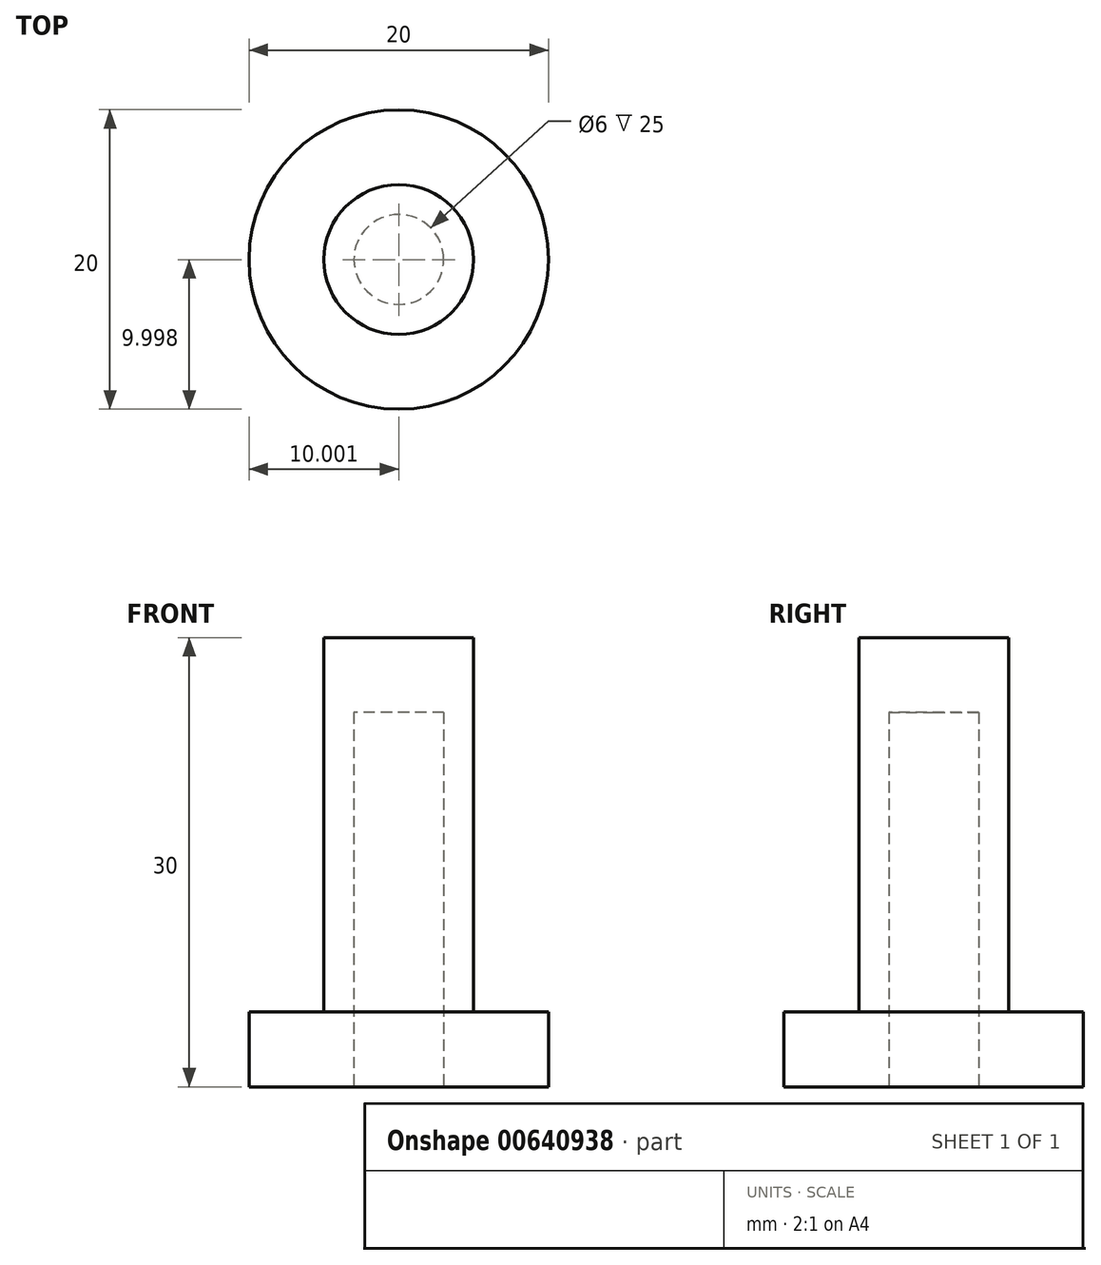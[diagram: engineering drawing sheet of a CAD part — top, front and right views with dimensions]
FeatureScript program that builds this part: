
annotation { "Feature Type Name" : "Feature", "Feature Type Description" : "" }
export const myFeature = defineFeature(function(context is Context, id is Id, definition is map)
    precondition{}
    {
        {
            var Q0;
            Q0=qCreatedBy(makeId("Top.planeOp"),FACE);
            var sketch = newSketch(context, id + "F0", { "sketchPlane" : qUnion([Q0])});
            skCircle(sketch, "E0", {"center": v(-26.7, 11.63) * mm, "radius": 3 * mm});
            skCircle(sketch, "E1", {"center": v(-26.7, 11.63) * mm, "radius": 5 * mm});
            skCircle(sketch, "E2", {"center": v(-26.7, 11.63) * mm, "radius": 10 * mm});
            skSolve(sketch);
        }
        {
            var Q0;
            Q0=makeQuery(id+"F0.imprint","IMPRINT",FACE,{"disambiguationData":[TD([[makeQuery(id+"F0.imprint","IMPRINT",EDGE,{"derivedFrom":sQuery(id+"F0.wireOp",EDGE,"E1")}),-1.0]])]});
            extrude(context, id + "F1", {"entities" : qUnion([Q0]), "depth" : 5 * mm, "offsetDistance" : 25 * mm});
        }
        {
            var Q0;
            Q0=makeQuery(id+"F0.imprint","IMPRINT",FACE,{"disambiguationData":[TD([[makeQuery(id+"F0.imprint","IMPRINT",EDGE,{"derivedFrom":sQuery(id+"F0.wireOp",EDGE,"E0")}),-1.0]])]});
            extrude(context, id + "F2", {"entities" : qUnion([Q0]), "operationType" : NewBodyOperationType.ADD, "depth" : 25 * mm, "offsetDistance" : 25 * mm});
        }
        {
            var Q0;
            Q0=makeQuery(id+"F2.opExtrude","CAP_FACE",FACE,{"disambiguationData":[OSD([sQuery(id+"F0.wireOp",EDGE,"E0"),sQuery(id+"F0.wireOp",EDGE,"E1")])],"isStart":false});
            var sketch = newSketch(context, id + "F3", { "sketchPlane" : qUnion([Q0])});
            skCircle(sketch, "E3", {"center": v(-26.7, 11.63) * mm, "radius": 5 * mm});
            skSolve(sketch);
        }
        {
            var Q0;
            Q0 = qSketchRegion(id + "F3", true);
            extrude(context, id + "F4", {"entities" : qUnion([Q0]), "operationType" : NewBodyOperationType.ADD, "depth" : 5 * mm, "offsetDistance" : 25 * mm});
        }
    });
